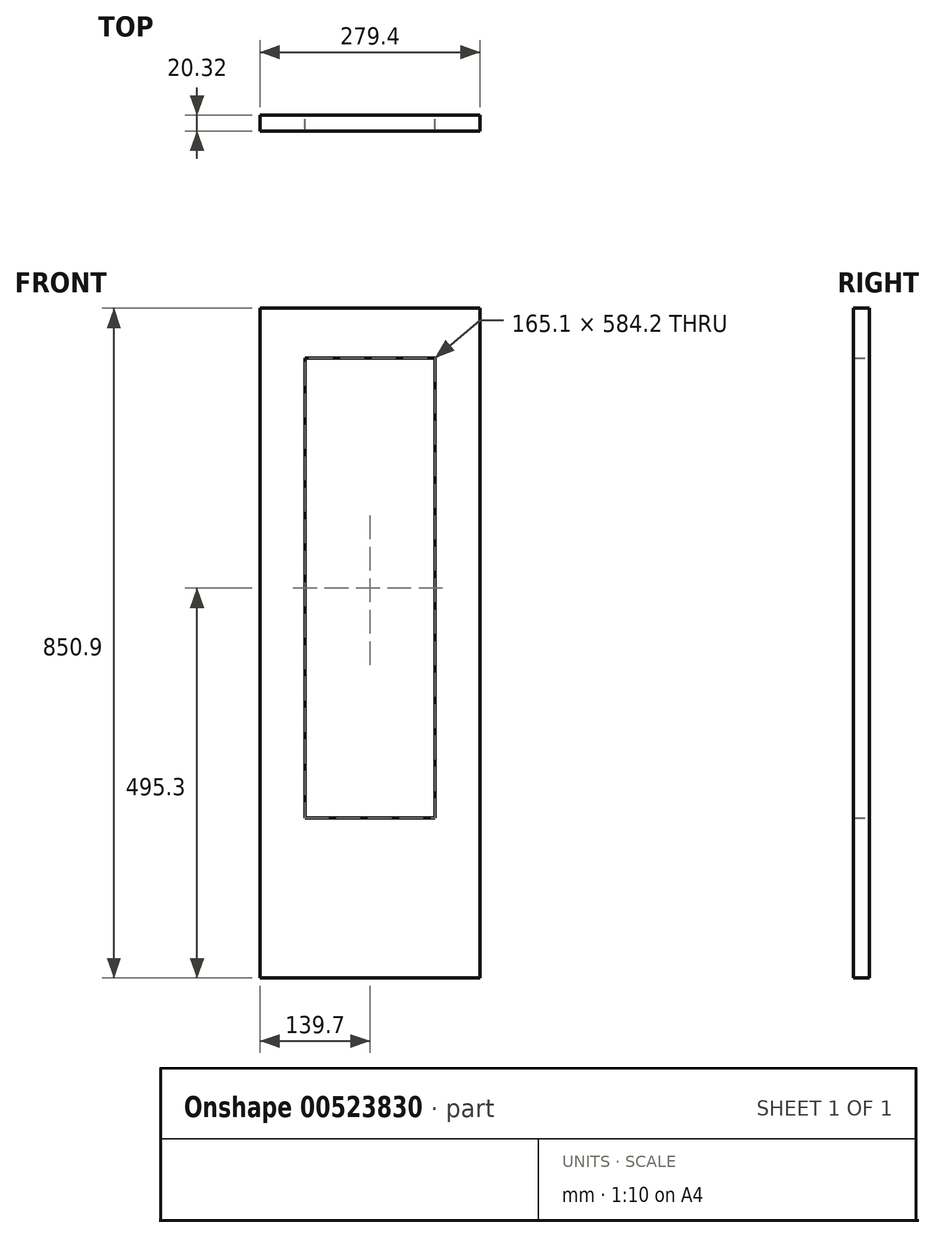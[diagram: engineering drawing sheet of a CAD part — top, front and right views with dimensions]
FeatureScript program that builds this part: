
annotation { "Feature Type Name" : "Feature", "Feature Type Description" : "" }
export const myFeature = defineFeature(function(context is Context, id is Id, definition is map)
    precondition{}
    {
        {
            var Q0;
            Q0=qCreatedBy(makeId("Front.planeOp"),FACE);
            var sketch = newSketch(context, id + "F0", { "sketchPlane" : qUnion([Q0])});
            skLineSegment(sketch, "E0.bottom", {"start": v(139.7, -425.45) * mm, "end": v(-139.7, -425.45) * mm});
            skLineSegment(sketch, "E0.top", {"start": v(139.7, 425.45) * mm, "end": v(-139.7, 425.45) * mm});
            skLineSegment(sketch, "E0.left", {"start": v(139.7, -425.45) * mm, "end": v(139.7, 425.45) * mm});
            skLineSegment(sketch, "E0.right", {"start": v(-139.7, -425.45) * mm, "end": v(-139.7, 425.45) * mm});
            skPoint(sketch, "E0.middle", {"position": v(0, 0) * mm});
            skLineSegment(sketch, "E1.bottom", {"start": v(-82.55, 361.95) * mm, "end": v(82.55, 361.95) * mm});
            skLineSegment(sketch, "E1.top", {"start": v(-82.55, -222.25) * mm, "end": v(82.55, -222.25) * mm});
            skLineSegment(sketch, "E1.left", {"start": v(-82.55, 361.95) * mm, "end": v(-82.55, -222.25) * mm});
            skLineSegment(sketch, "E1.right", {"start": v(82.55, 361.95) * mm, "end": v(82.55, -222.25) * mm});
            skSolve(sketch);
        }
        {
            var Q0;
            Q0=makeQuery(id+"F0.imprint","IMPRINT",FACE,{"disambiguationData":[TD([[makeQuery(id+"F0.imprint","IMPRINT",EDGE,{"derivedFrom":sQuery(id+"F0.wireOp",EDGE,"E0.bottom")}),-1.0]])]});
            extrude(context, id + "F1", {"entities" : qUnion([Q0]), "depth" : 20.32 * mm, "offsetDistance" : 25.4 * mm});
        }
    });
